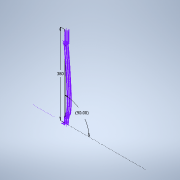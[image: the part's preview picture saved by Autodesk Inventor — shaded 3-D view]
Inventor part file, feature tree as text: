
AUTODESK INVENTOR PART (.ipt)
format: ipt  version: 2022 (Build 260153000, 153)  size: 327,168 bytes
history: native  units: mm
features: sketch x5, sweep x1
ambient origin geometry x8: Origin, YZ Plane, XZ Plane, XY Plane, X Axis, Y Axis, Z Axis, Center Point
bodies: Solid1 (feature_tree)
feature tree (6):
  sketch  "Sketch1"  dims[d0=380.0mm d1=90.0deg]
  sketch  "Sketch2"  dims[d8=330.0mm]
  sketch  "3D Sketch1"
  sweep  "Sweep2"
  sketch  "Sketch3"  dims[d9=90.0deg d10=0.0mm d11=0.0mm]
  sketch  "3D Sketch2"
